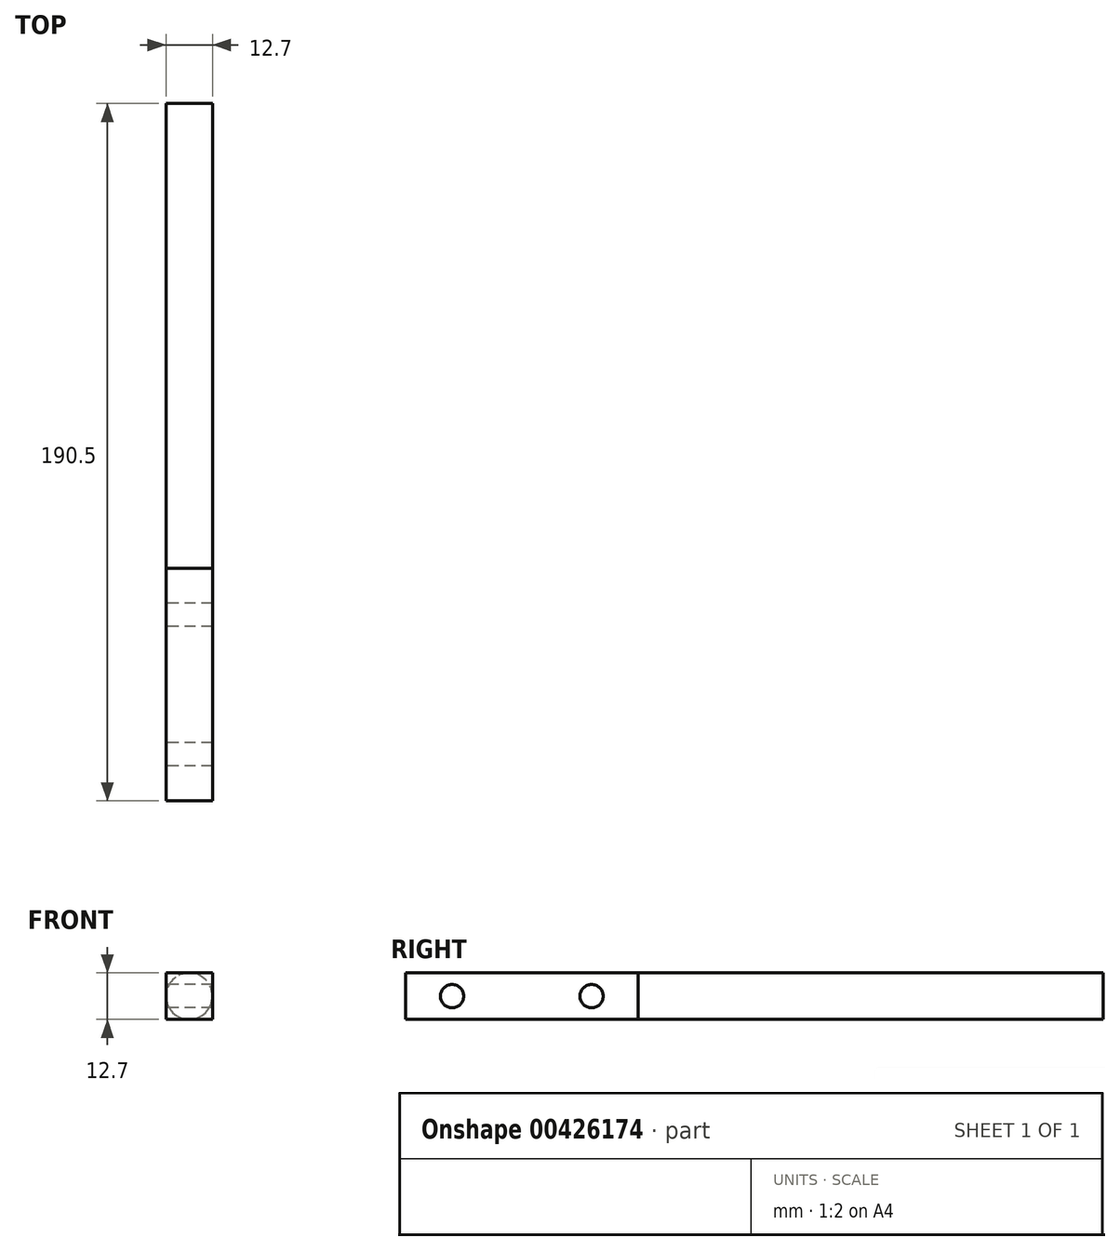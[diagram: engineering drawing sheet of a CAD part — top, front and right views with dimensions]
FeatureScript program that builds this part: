
annotation { "Feature Type Name" : "Feature", "Feature Type Description" : "" }
export const myFeature = defineFeature(function(context is Context, id is Id, definition is map)
    precondition{}
    {
        {
            var Q0;
            Q0=qCreatedBy(makeId("Right.planeOp"),FACE);
            var sketch = newSketch(context, id + "F0", { "sketchPlane" : qUnion([Q0])});
            skLineSegment(sketch, "E0.bottom", {"start": v(-63.5, 12.7) * mm, "end": v(0, 12.7) * mm});
            skLineSegment(sketch, "E0.top", {"start": v(-63.5, 0) * mm, "end": v(0, 0) * mm});
            skLineSegment(sketch, "E0.left", {"start": v(-63.5, 12.7) * mm, "end": v(-63.5, 0) * mm});
            skLineSegment(sketch, "E0.right", {"start": v(0, 12.7) * mm, "end": v(0, 0) * mm});
            skCircle(sketch, "E1", {"center": v(-50.8, 6.35) * mm, "radius": 3.18 * mm});
            skCircle(sketch, "E2", {"center": v(-12.7, 6.35) * mm, "radius": 3.18 * mm});
            skSolve(sketch);
        }
        {
            var Q0;
            Q0 = qSketchRegion(id + "F0", true);
            extrude(context, id + "F1", {"entities" : qUnion([Q0]), "depth" : 12.7 * mm});
        }
        {
            var Q0;
            Q0=makeQuery(id+"F1.opExtrude","SWEPT_FACE",FACE,{"disambiguationData":[OSD([sQuery(id+"F0.wireOp",EDGE,"E0.right")])]});
            var sketch = newSketch(context, id + "F2", { "sketchPlane" : qUnion([Q0])});
            skCircle(sketch, "E3", {"center": v(-6.35, 6.35) * mm, "radius": 6.35 * mm});
            skPoint(sketch, "E3.centerSnap0", {"position": v(0, 6.35) * mm});
            skSolve(sketch);
        }
        {
            var Q0;
            Q0 = qSketchRegion(id + "F2", true);
            extrude(context, id + "F3", {"entities" : qUnion([Q0]), "operationType" : NewBodyOperationType.ADD, "depth" : 127 * mm});
        }
    });
